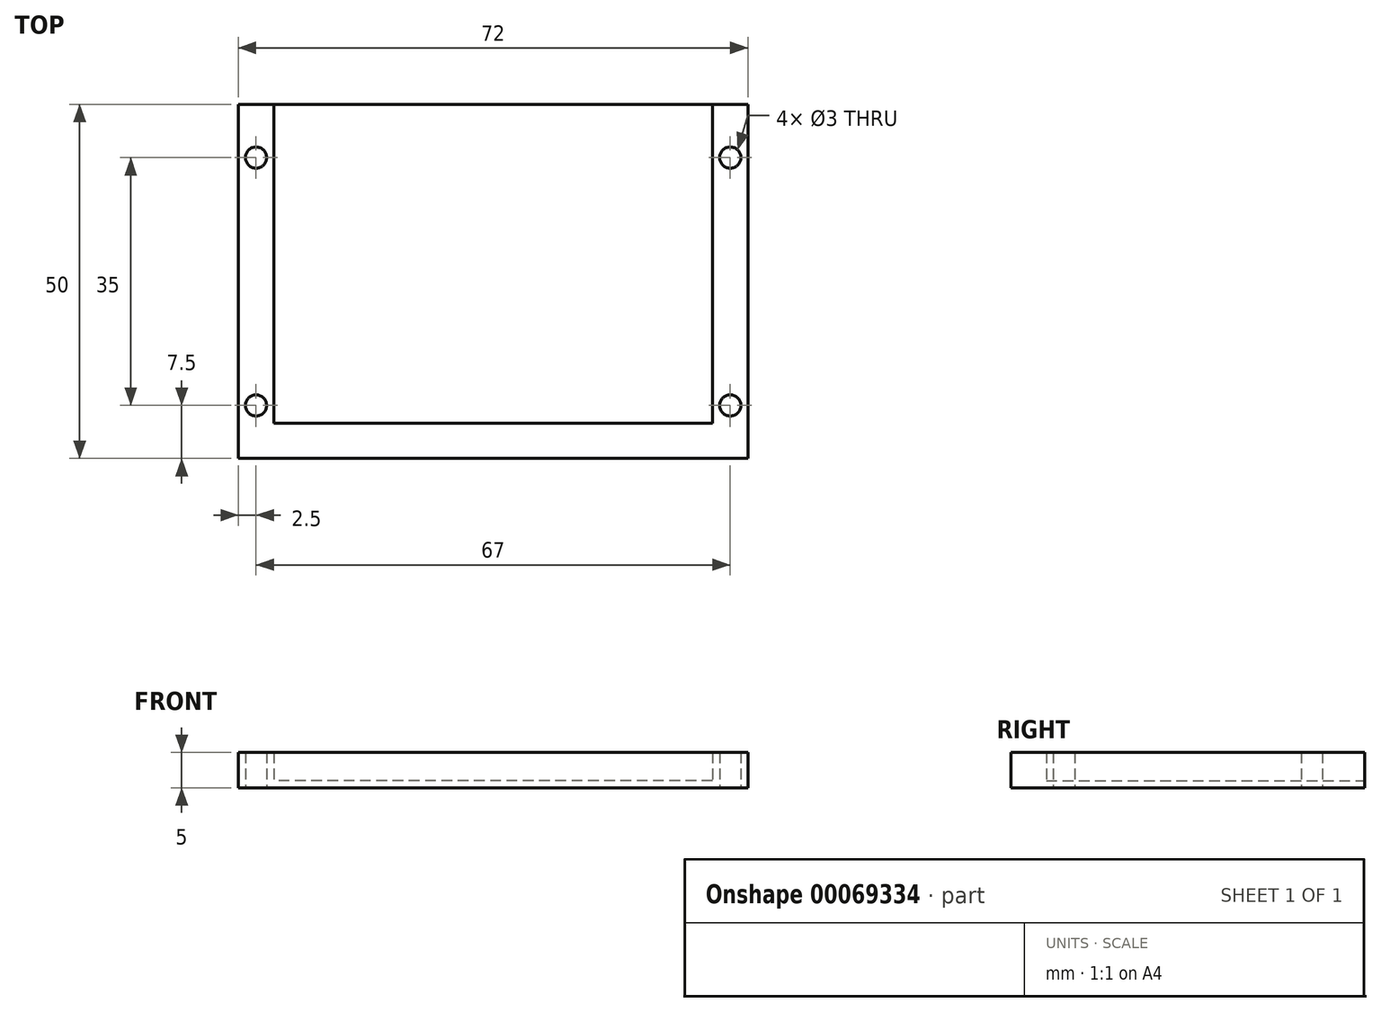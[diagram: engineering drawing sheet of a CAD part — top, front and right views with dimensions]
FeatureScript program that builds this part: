
annotation { "Feature Type Name" : "Feature", "Feature Type Description" : "" }
export const myFeature = defineFeature(function(context is Context, id is Id, definition is map)
    precondition{}
    {
        {
            var Q0;
            Q0=qCreatedBy(makeId("Top.planeOp"),FACE);
            var sketch = newSketch(context, id + "F0", { "sketchPlane" : qUnion([Q0])});
            skLineSegment(sketch, "E0", {"start": v(-53.17, 0) * mm, "end": v(56.7, 0) * mm, "construction": true});
            skLineSegment(sketch, "E1.0", {"start": v(-53.17, -20) * mm, "end": v(56.7, -20) * mm, "construction": true});
            skLineSegment(sketch, "E2.0", {"start": v(-53.17, -25) * mm, "end": v(56.7, -25) * mm, "construction": true});
            skLineSegment(sketch, "E3", {"start": v(0, 43.47) * mm, "end": v(0, -45.23) * mm, "construction": true});
            skLineSegment(sketch, "E4.0", {"start": v(-36, 0) * mm, "end": v(-36, -45.23) * mm, "construction": true});
            skLineSegment(sketch, "E5.0", {"start": v(-31, 0) * mm, "end": v(-31, -45.23) * mm, "construction": true});
            skLineSegment(sketch, "E6", {"start": v(-36, 0) * mm, "end": v(-36, -25) * mm});
            skLineSegment(sketch, "E7", {"start": v(-36, -25) * mm, "end": v(0, -25) * mm});
            skPoint(sketch, "E7.endSnap0", {"position": v(1.76, -25) * mm});
            skLineSegment(sketch, "E8", {"start": v(-31, 0) * mm, "end": v(-31, -20) * mm});
            skLineSegment(sketch, "E9", {"start": v(-31, -20) * mm, "end": v(0, -20) * mm});
            skLineSegment(sketch, "E10.MirrorCS", {"start": v(31, 0) * mm, "end": v(31, -20) * mm});
            skLineSegment(sketch, "E11.MirrorCS", {"start": v(31, -20) * mm, "end": v(0, -20) * mm});
            skLineSegment(sketch, "E12.MirrorCS", {"start": v(36, -25) * mm, "end": v(0, -25) * mm});
            skLineSegment(sketch, "E13.MirrorCS", {"start": v(36, 0) * mm, "end": v(36, -25) * mm});
            skLineSegment(sketch, "E14.MirrorCS", {"start": v(36, 0) * mm, "end": v(36, 25) * mm});
            skLineSegment(sketch, "E15.MirrorCS", {"start": v(36, 25) * mm, "end": v(0, 25) * mm});
            skLineSegment(sketch, "E16.MirrorCS", {"start": v(-36, 25) * mm, "end": v(0, 25) * mm});
            skLineSegment(sketch, "E17.MirrorCS", {"start": v(-36, 0) * mm, "end": v(-36, 25) * mm});
            skLineSegment(sketch, "E18.MirrorCS", {"start": v(-31, 0) * mm, "end": v(-31, 20) * mm});
            skLineSegment(sketch, "E19.MirrorCS", {"start": v(31, 0) * mm, "end": v(31, 20) * mm});
            skLineSegment(sketch, "E20", {"start": v(-31, 20) * mm, "end": v(-31, 25) * mm});
            skLineSegment(sketch, "E21", {"start": v(31, 20) * mm, "end": v(31, 25) * mm});
            skLineSegment(sketch, "E22.0", {"start": v(-36, -17.5) * mm, "end": v(-31, -17.5) * mm, "construction": true});
            skCircle(sketch, "E23", {"center": v(-33.5, -17.5) * mm, "radius": 1.5 * mm});
            skCircle(sketch, "E24.MirrorC", {"center": v(33.5, -17.5) * mm, "radius": 1.5 * mm});
            skCircle(sketch, "E25.MirrorC", {"center": v(33.5, 17.5) * mm, "radius": 1.5 * mm});
            skCircle(sketch, "E26.MirrorC", {"center": v(-33.5, 17.5) * mm, "radius": 1.5 * mm});
            skSolve(sketch);
        }
        {
            var Q0;
            Q0=makeQuery(id+"F0.imprint","IMPRINT",FACE,{"disambiguationData":[TD([[makeQuery(id+"F0.imprint","IMPRINT",EDGE,{"derivedFrom":sQuery(id+"F0.wireOp",EDGE,"E8")}),1.0]])]});
            extrude(context, id + "F1", {"entities" : qUnion([Q0]), "depth" : 1 * mm});
        }
        {
            var Q0;
            Q0=makeQuery(id+"F0.imprint","IMPRINT",FACE,{"disambiguationData":[TD([[makeQuery(id+"F0.imprint","IMPRINT",EDGE,{"derivedFrom":sQuery(id+"F0.wireOp",EDGE,"E6")}),1.0]])]});
            extrude(context, id + "F2", {"entities" : qUnion([Q0]), "operationType" : NewBodyOperationType.ADD, "depth" : 5 * mm});
        }
    });
